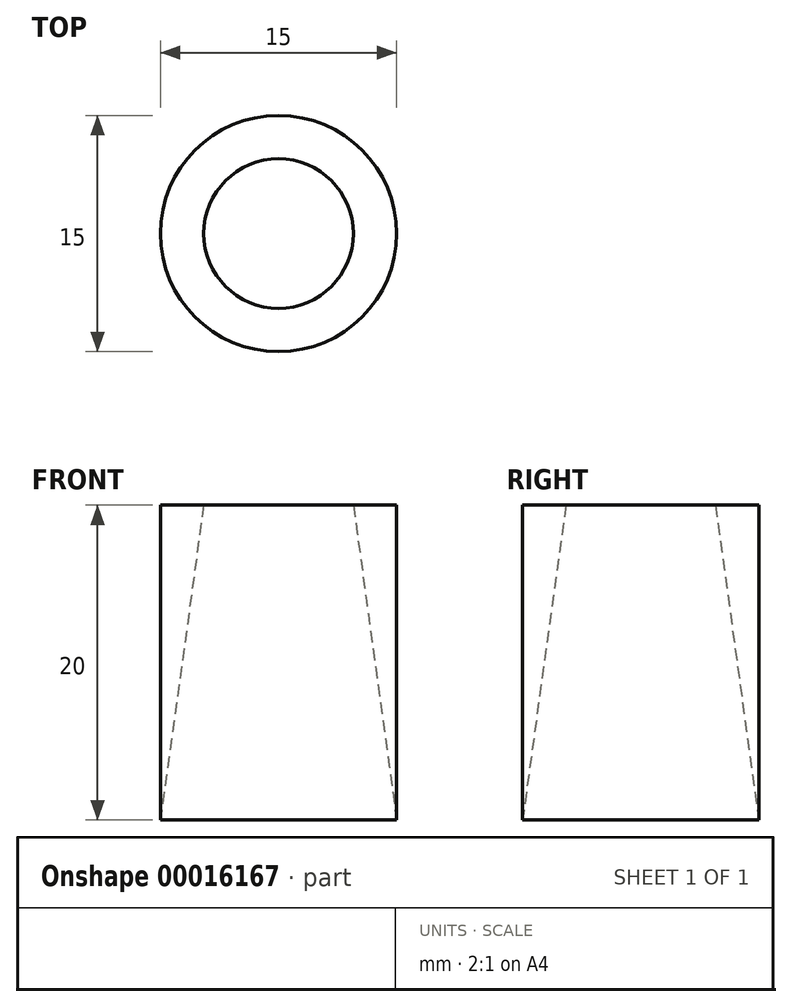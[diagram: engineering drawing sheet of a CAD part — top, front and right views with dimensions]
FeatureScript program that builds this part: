
annotation { "Feature Type Name" : "Feature", "Feature Type Description" : "" }
export const myFeature = defineFeature(function(context is Context, id is Id, definition is map)
    precondition{}
    {
        {
            var Q0;
            Q0=qCreatedBy(makeId("Top.planeOp"),FACE);
            var sketch = newSketch(context, id + "F0", { "sketchPlane" : qUnion([Q0])});
            skCircle(sketch, "E0", {"center": v(0, 0) * mm, "radius": 7.5 * mm});
            skSolve(sketch);
        }
        {
            var Q0;
            Q0 = qSketchRegion(id + "F0", true);
            extrude(context, id + "F1", {"entities" : qUnion([Q0]), "depth" : 20 * mm});
        }
        {
            var Q0;
            Q0=makeQuery(id+"F1.opExtrude","CAP_FACE",FACE,{"disambiguationData":[OSD([sQuery(id+"F0.wireOp",EDGE,"E0")])],"isStart":false});
            var sketch = newSketch(context, id + "F2", { "sketchPlane" : qUnion([Q0])});
            skCircle(sketch, "E1", {"center": v(0, 0) * mm, "radius": 4.75 * mm});
            skSolve(sketch);
        }
        {
            var Q1;
            Q1=makeQuery(id+"F2.imprint","IMPRINT",FACE,{"disambiguationData":[TD([[makeQuery(id+"F2.imprint","IMPRINT",EDGE,{"derivedFrom":sQuery(id+"F2.wireOp",EDGE,"E1")}),1.0]])]});
            var Q2;
            Q2=makeQuery(id+"F1.opExtrude","CAP_FACE",FACE,{"disambiguationData":[OSD([sQuery(id+"F0.wireOp",EDGE,"E0")])],"isStart":true});
            loft(context, id + "F3", {"operationType" : NewBodyOperationType.REMOVE, "sheetProfilesArray" : [{ "sheetProfileEntities" : qUnion([Q1]) }, { "sheetProfileEntities" : qUnion([Q2]) }]});
        }
    });
